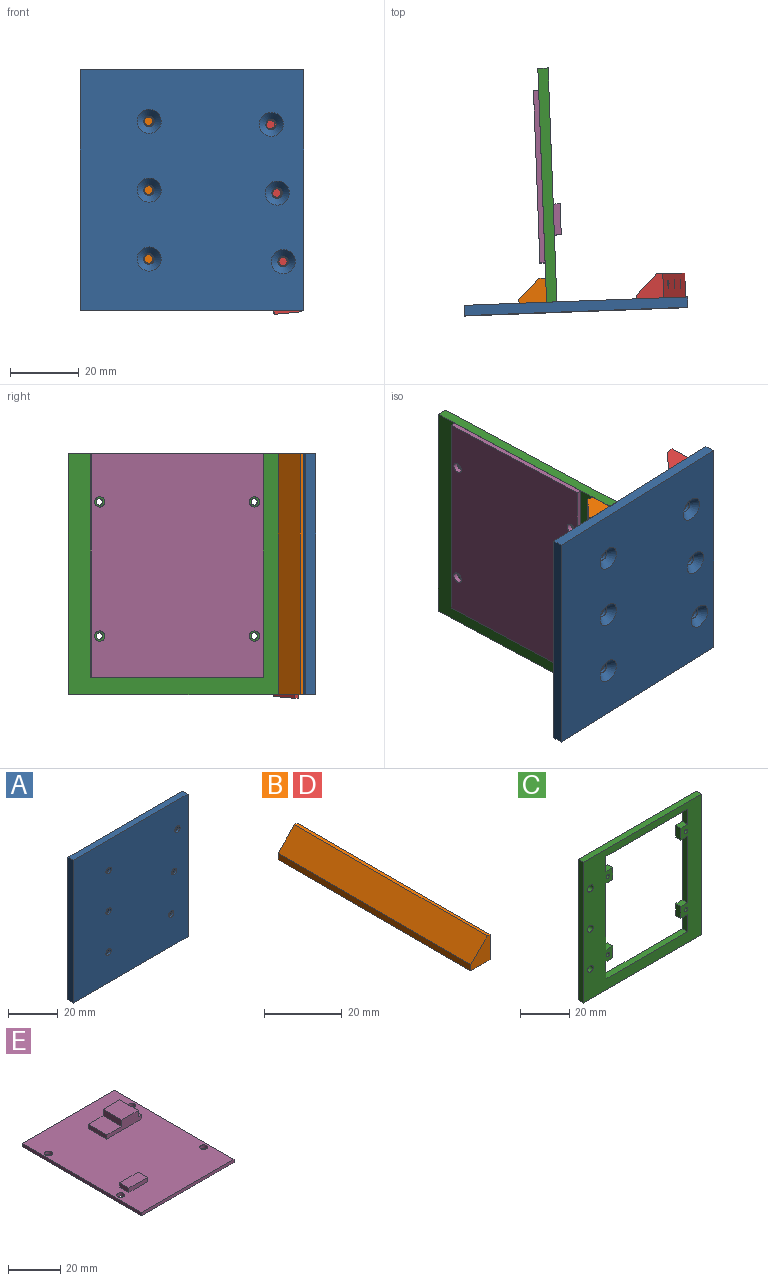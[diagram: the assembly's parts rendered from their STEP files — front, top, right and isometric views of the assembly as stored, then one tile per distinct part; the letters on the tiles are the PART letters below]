
ASSEMBLY  parts=5 mates=3
PART A: 18 faces, bbox 65x3x70 mm
  f0: plane 65x3mm, normal (0,0,1), area 195mm2, adj f1,f9,f10,f11
  f1: plane 70x3mm, normal (-1,0,0), area 210mm2, adj f0,f2,f10,f11
  f2: plane 65x3mm, normal (0,0,-1), area 195mm2, adj f1,f9,f10,f11
  f3: cylinder r=1.5mm len=3mm, axis (0,1,0), area 9.4mm2, adj f10,f16
  f4: cylinder r=1.5mm len=3mm, axis (0,1,0), area 9.4mm2, adj f10,f14
  f5: cylinder r=1.5mm len=3mm, axis (0,1,0), area 9.4mm2, adj f10,f13
  f6: cylinder r=1.5mm len=3mm, axis (0,1,0), area 9.4mm2, adj f10,f17
  f7: cylinder r=1.5mm len=3mm, axis (0,1,0), area 9.4mm2, adj f10,f12
  f8: cylinder r=1.5mm len=3mm, axis (0,1,0), area 9.4mm2, adj f10,f15
  f9: plane 70x3mm, normal (1,0,0), area 210mm2, adj f0,f2,f10,f11
  f10: plane 70x65mm, normal (0,-1,0), area 4507.6mm2, adj f0,f1,f2,f3,f4,f5,f6,f7
  f11: plane 70x65mm, normal (0,1,0), area 4319.1mm2, adj f0,f1,f2,f9,f12,f13,f14,f15
  f12: cone r=3.5mm half-angle=45deg, axis (0,1,0), area 44.4mm2, adj f7,f11
  f13: cone r=3.5mm half-angle=45deg, axis (0,1,0), area 44.4mm2, adj f5,f11
  f14: cone r=3.5mm half-angle=45deg, axis (0,1,0), area 44.4mm2, adj f4,f11
  f15: cone r=3.5mm half-angle=45deg, axis (0,1,0), area 44.4mm2, adj f8,f11
  f16: cone r=3.5mm half-angle=45deg, axis (0,1,0), area 44.4mm2, adj f3,f11
  f17: cone r=3.5mm half-angle=45deg, axis (0,1,0), area 44.4mm2, adj f6,f11
PART B: 24 faces, bbox 7x70x8 mm
  f0: plane 70x7mm, normal (0,0,-1), area 475.2mm2, adj f1,f2,f3,f4,f13,f15,f17,f19
  f1: plane 70x2mm, normal (-1,0,0), area 140mm2, adj f0,f2,f4,f6
  f2: plane 8x7mm, normal (0,-1,0), area 38mm2, adj f0,f1,f3,f5,f6
  f3: plane 70x8mm, normal (1,0,0), area 545.3mm2, adj f0,f2,f4,f5,f7,f9,f11
  f4: plane 8x7mm, normal (0,1,0), area 38mm2, adj f0,f1,f3,f5,f6
  f5: plane 70x1mm, normal (0,0,1), area 70mm2, adj f2,f3,f4,f6
  f6: plane 70x6mm, normal (-0.71,0,0.71), area 594mm2, adj f1,f2,f4,f5
  f7: cylinder r=1.25mm len=2.7mm, axis (1,0,0), area 21.2mm2, adj f3,f8
  f8: plane 2.5x2.5mm, normal (1,0,0), area 4.9mm2, adj f7
  f9: cylinder r=1.25mm len=2.7mm, axis (1,0,0), area 21.2mm2, adj f3,f10
  f10: plane 2.5x2.5mm, normal (1,0,0), area 4.9mm2, adj f9
  f11: cylinder r=1.25mm len=2.7mm, axis (1,0,0), area 21.2mm2, adj f3,f12
  f12: plane 2.5x2.5mm, normal (1,0,0), area 4.9mm2, adj f11
  f13: cylinder r=1.25mm len=2.7mm, axis (0,0,-1), area 21.2mm2, adj f0,f14
  f14: plane 2.5x2.5mm, normal (0,0,-1), area 4.9mm2, adj f13
  f15: cylinder r=1.25mm len=2.7mm, axis (0,0,-1), area 21.2mm2, adj f0,f16
  f16: plane 2.5x2.5mm, normal (0,0,-1), area 4.9mm2, adj f15
  f17: cylinder r=1.25mm len=2.7mm, axis (0,0,-1), area 21.2mm2, adj f0,f18
  f18: plane 2.5x2.5mm, normal (0,0,-1), area 4.9mm2, adj f17
  f19: plane 0.2x0.15mm, normal (0,-1,0), area 0mm2, adj f0,f20,f22,f23
  f20: plane 0.5x0.15mm, normal (-1,0,0), area 0.1mm2, adj f0,f19,f21,f23
  f21: plane 0.2x0.15mm, normal (0,1,0), area 0mm2, adj f0,f20,f22,f23
  f22: plane 0.5x0.15mm, normal (1,0,0), area 0.1mm2, adj f0,f19,f21,f23
  f23: plane 0.5x0.2mm, normal (0,0,-1), area 0.1mm2, adj f19,f20,f21,f22
PART C: 33 faces, bbox 68x3x70 mm
  f0: plane 68x3mm, normal (0,0,1), area 204mm2, adj f1,f30,f31,f32
  f1: plane 70x3mm, normal (-1,0,0), area 210mm2, adj f0,f2,f31,f32
  f2: plane 68x3mm, normal (0,0,-1), area 204mm2, adj f1,f30,f31,f32
  f3: plane 3.9x3mm, normal (0,0,-1), area 11.7mm2, adj f4,f29,f31,f32
  f4: plane 8.52x3mm, normal (-1,0,0), area 25.6mm2, adj f3,f5,f31,f32
  f5: plane 47x3mm, normal (0,0,1), area 141mm2, adj f4,f6,f31,f32
  f6: plane 8.55x3mm, normal (1,0,0), area 25.6mm2, adj f5,f7,f31,f32
  f7: plane 4x3mm, normal (0,0,-1), area 12mm2, adj f6,f8,f31,f32
  f8: plane 5.87x3mm, normal (1,0,0), area 17.6mm2, adj f7,f9,f31,f32
  f9: plane 4x3mm, normal (0,0,1), area 12mm2, adj f8,f10,f31,f32
  f10: plane 33.1x3mm, normal (1,0,0), area 99.3mm2, adj f9,f11,f31,f32
  f11: plane 4x3mm, normal (0,0,-1), area 12mm2, adj f10,f12,f31,f32
  f12: plane 5.93x3mm, normal (1,0,0), area 17.8mm2, adj f11,f13,f31,f32
  f13: plane 4x3mm, normal (0,0,1), area 12mm2, adj f12,f14,f31,f32
  f14: plane 7.55x3mm, normal (1,0,0), area 22.7mm2, adj f13,f15,f31,f32
  f15: plane 47x3mm, normal (0,0,-1), area 141mm2, adj f14,f16,f31,f32
  f16: plane 7.58x3mm, normal (-1,0,0), area 22.7mm2, adj f15,f17,f31,f32
  f17: plane 3.9x3mm, normal (0,0,1), area 11.7mm2, adj f16,f18,f31,f32
  f18: plane 5.9x3mm, normal (-1,0,0), area 17.7mm2, adj f17,f19,f31,f32
  f19: plane 3.9x3mm, normal (0,0,-1), area 11.7mm2, adj f18,f20,f31,f32
  f20: plane 33.1x3mm, normal (-1,0,0), area 99.3mm2, adj f19,f21,f31,f32
  f21: plane 3.9x3mm, normal (0,0,1), area 11.7mm2, adj f20,f29,f31,f32
  f22: cylinder r=0.95mm len=3mm, axis (0,1,0), area 17.9mm2, adj f31,f32
  f23: cylinder r=0.95mm len=3mm, axis (0,1,0), area 17.9mm2, adj f31,f32
  f24: cylinder r=0.95mm len=3mm, axis (0,1,0), area 17.9mm2, adj f31,f32
  f25: cylinder r=0.95mm len=3mm, axis (0,1,0), area 17.9mm2, adj f31,f32
  f26: cylinder r=1.6mm len=3.2mm, axis (0,1,0), area 30.2mm2, adj f31,f32
  f27: cylinder r=1.6mm len=3.2mm, axis (0,1,0), area 30.2mm2, adj f31,f32
  f28: cylinder r=1.6mm len=3.2mm, axis (0,1,0), area 30.2mm2, adj f31,f32
  f29: plane 5.9x3mm, normal (-1,0,0), area 17.7mm2, adj f3,f21,f31,f32
  f30: plane 70x3mm, normal (1,0,0), area 210mm2, adj f0,f2,f31,f32
  f31: plane 70x68mm, normal (0,-1,0), area 1950.8mm2, adj f0,f1,f2,f3,f4,f5,f6,f7
  f32: plane 70x68mm, normal (0,1,0), area 1950.8mm2, adj f0,f1,f2,f3,f4,f5,f6,f7
PART D: same geometry as B
PART E: 24 faces, bbox 50x65x6.5 mm
  f0: plane 65x50mm, normal (0,0,1), area 2981.7mm2, adj f1,f2,f3,f4,f5,f6,f7,f8
  f1: plane 65x1.5mm, normal (-1,0,0), area 97.5mm2, adj f0,f2,f7,f9
  f2: plane 50x1.5mm, normal (0,-1,0), area 75mm2, adj f0,f1,f3,f9
  f3: plane 65x1.5mm, normal (1,0,0), area 97.5mm2, adj f0,f2,f7,f9
  f4: cylinder r=1.5mm len=3mm, axis (0,0,-1), area 14.1mm2, adj f0,f9
  f5: cylinder r=1.5mm len=3mm, axis (0,0,-1), area 14.1mm2, adj f0,f9
  f6: cylinder r=1.5mm len=3mm, axis (0,0,-1), area 14.1mm2, adj f0,f9
  f7: plane 50x1.5mm, normal (0,1,0), area 75mm2, adj f0,f1,f3,f9
  f8: cylinder r=1.5mm len=3mm, axis (0,0,-1), area 14.1mm2, adj f0,f9
  f9: plane 65x50mm, normal (0,0,-1), area 3221.7mm2, adj f1,f2,f3,f4,f5,f6,f7,f8
  f10: plane 10x2mm, normal (0,1,0), area 20mm2, adj f0,f11,f13,f14
  f11: plane 5x2mm, normal (-1,0,0), area 10mm2, adj f0,f10,f12,f14
  f12: plane 10x2mm, normal (0,-1,0), area 20mm2, adj f0,f11,f13,f14
  f13: plane 5x2mm, normal (1,0,0), area 10mm2, adj f0,f10,f12,f14
  f14: plane 10x5mm, normal (0,0,1), area 50mm2, adj f10,f11,f12,f13
  f15: plane 10x3mm, normal (1,0,0), area 30mm2, adj f16,f18,f19,f23
  f16: plane 19x5mm, normal (0,1,0), area 65mm2, adj f0,f15,f17,f19,f20,f21,f22,f23
  f17: plane 10x3mm, normal (-1,0,0), area 30mm2, adj f16,f18,f19,f21
  f18: plane 19x5mm, normal (0,-1,0), area 65mm2, adj f0,f15,f17,f19,f20,f21,f22,f23
  f19: plane 10x9mm, normal (0,0,1), area 90mm2, adj f15,f16,f17,f18
  f20: plane 10x2mm, normal (-1,0,0), area 20mm2, adj f0,f16,f18,f21
  f21: plane 10x8mm, normal (0,0,1), area 80mm2, adj f16,f17,f18,f20
  f22: plane 10x2mm, normal (1,0,0), area 20mm2, adj f0,f16,f18,f23
  f23: plane 10x2mm, normal (0,0,1), area 20mm2, adj f15,f16,f18,f22
PLACE A rot(axis=(1,0.02,0),180deg) t=(62.2,40.75,-25.94)mm
PLACE B rot(axis=(0.59,-0.57,-0.57),118.8deg) t=(59.79,35.9,-16.64)mm
PLACE C rot(axis=(0,0,1),92.1deg) t=(58.36,74.09,-11.39)mm
PLACE D rot(axis=(0.61,-0.59,-0.54),121.9deg) t=(96.71,37.28,-17.14)mm
PLACE E rot(axis=(-0.59,0.57,-0.57),118.8deg) t=(56.58,81.32,-5.48)mm
MATE fastened E.f6 <-> C.f25  axis (1,0.04,0) through (58.97,57.64,-37.81)mm
MATE fastened C.f27 <-> B.f15  axis (-1,-0.04,0) through (59.35,47.64,-19.81)mm
MATE fastened B.f9 <-> A.f4  axis (0.04,-1,0) through (55.5,43.5,-19.81)mm
